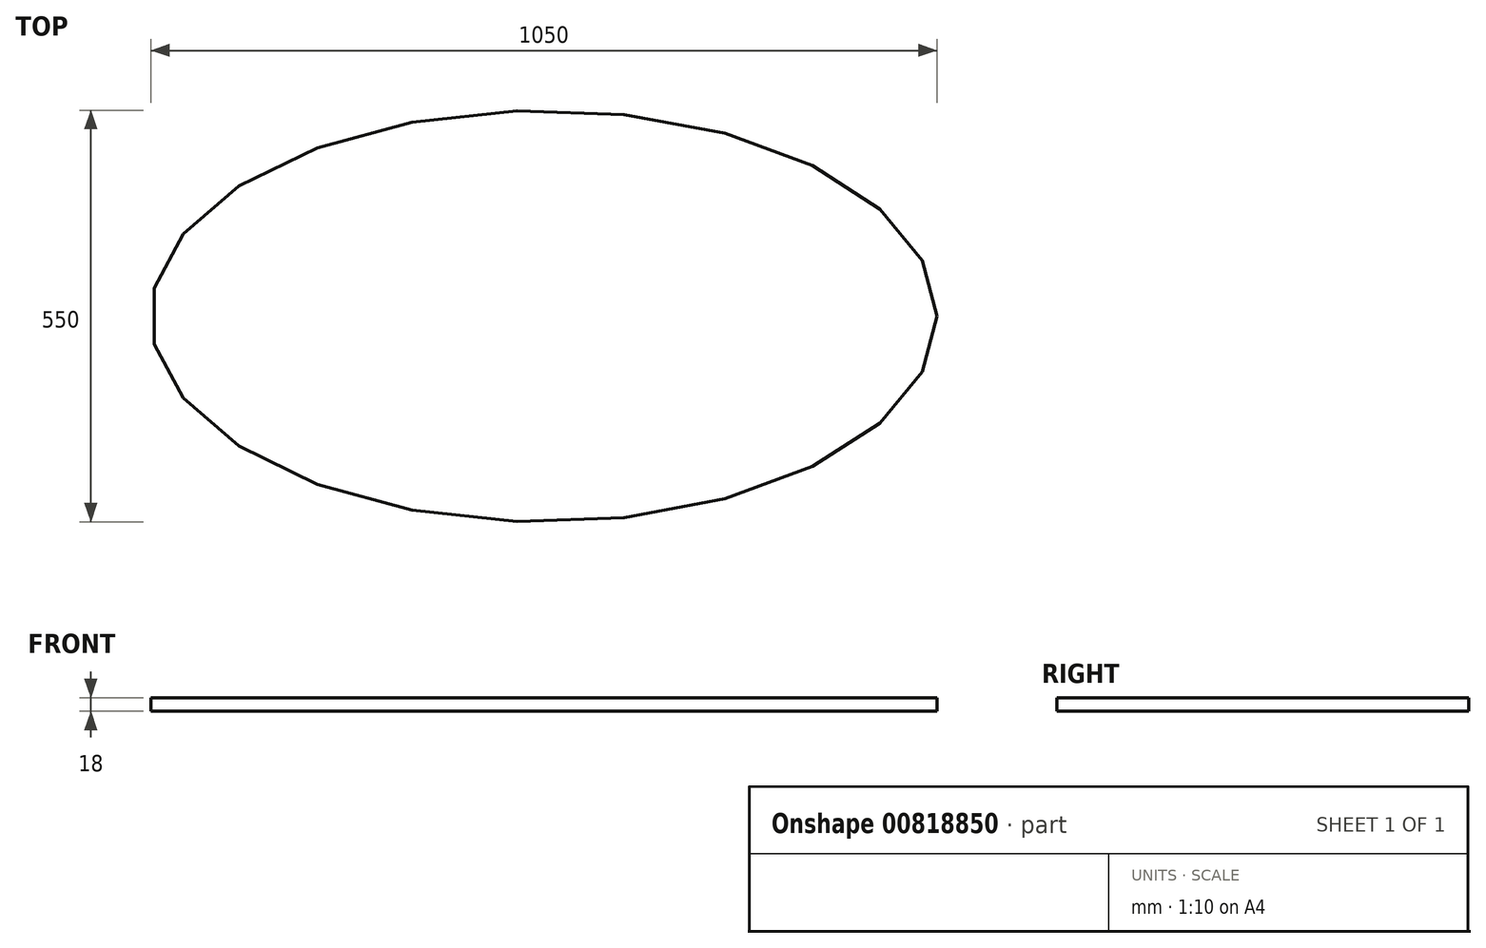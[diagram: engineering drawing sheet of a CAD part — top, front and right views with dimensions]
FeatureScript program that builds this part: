
annotation { "Feature Type Name" : "Feature", "Feature Type Description" : "" }
export const myFeature = defineFeature(function(context is Context, id is Id, definition is map)
    precondition{}
    {
        {
            var Q0;
            Q0=qCreatedBy(makeId("Top.planeOp"),FACE);
            var sketch = newSketch(context, id + "F0", { "sketchPlane" : qUnion([Q0])});
            skEllipse(sketch, "E0", {"center": v(0, 0) * mm, "majorRadius": 525 * mm, "minorRadius": 275 * mm, "majorAxis": v(1, 0)});
            skSolve(sketch);
        }
        {
            var Q0;
            Q0 = qSketchRegion(id + "F0", true);
            extrude(context, id + "F1", {"entities" : qUnion([Q0]), "depth" : 18 * mm, "offsetDistance" : 25 * mm});
        }
    });
